# Revit family: STS-709M_RV17_LOD_400
name_source: partatom
category: Электрооборудование
revit_build: Autodesk Revit 2017 (Build: 20170118_1100(x64)
units: mm (PartAtom-declared; Revit-internal decimal feet)

## family parameters
Всегда вертикально = Да
Конфигурация панели = Два столбца, слева направо
На основе рабочей плоскости = Да
Общий = Нет
При загрузке вырезать с полостями = Нет
Размер круглого соединителя = Использовать диаметр
Тип детали = Щит
Точка расчета площади = Нет

## types (1)
- STS-709M
    ADSK_URL страницы изделия = https://stilsoft.ru
    ADSK_Единица измерения = шт.
    ADSK_Завод-изготовитель = ООО «Основа Безопасности»
    ADSK_Количество = 1
    ADSK_Марка = СТВФ.431295.004-01
    ADSK_Масса = 0.1
    ADSK_Наименование = STS-709М
    ADSK_Размер_Высота = 12 мм
    ADSK_Размер_Длина = 105 мм
    ADSK_Размер_Ширина = 72 мм
    Дальность чтения / записи, см = 4-6
    Диапазон рабочих температур, = от +5 до +50
    Интерфейс связи с компьютером = USB 2.0
    Напряжение = 5
    Напряжение питание постоянного тока, не = 5 (USB)
    Отметка по умолчанию = 1219 мм
    Потребляемый ток, не более, А = 0 А
    Рабочая частота, кГц = 13.56
    Удалённость считывателя от компьютера, = 3 мм
    Форматы считывателя (1) = MIFARE Ultralight
    Форматы считывателя (2) = MIFARE Standard 1k
    Форматы считывателя (3) = MIFARE Standard 4k
    Форматы считывателя (4) = MIFARE DESFire
